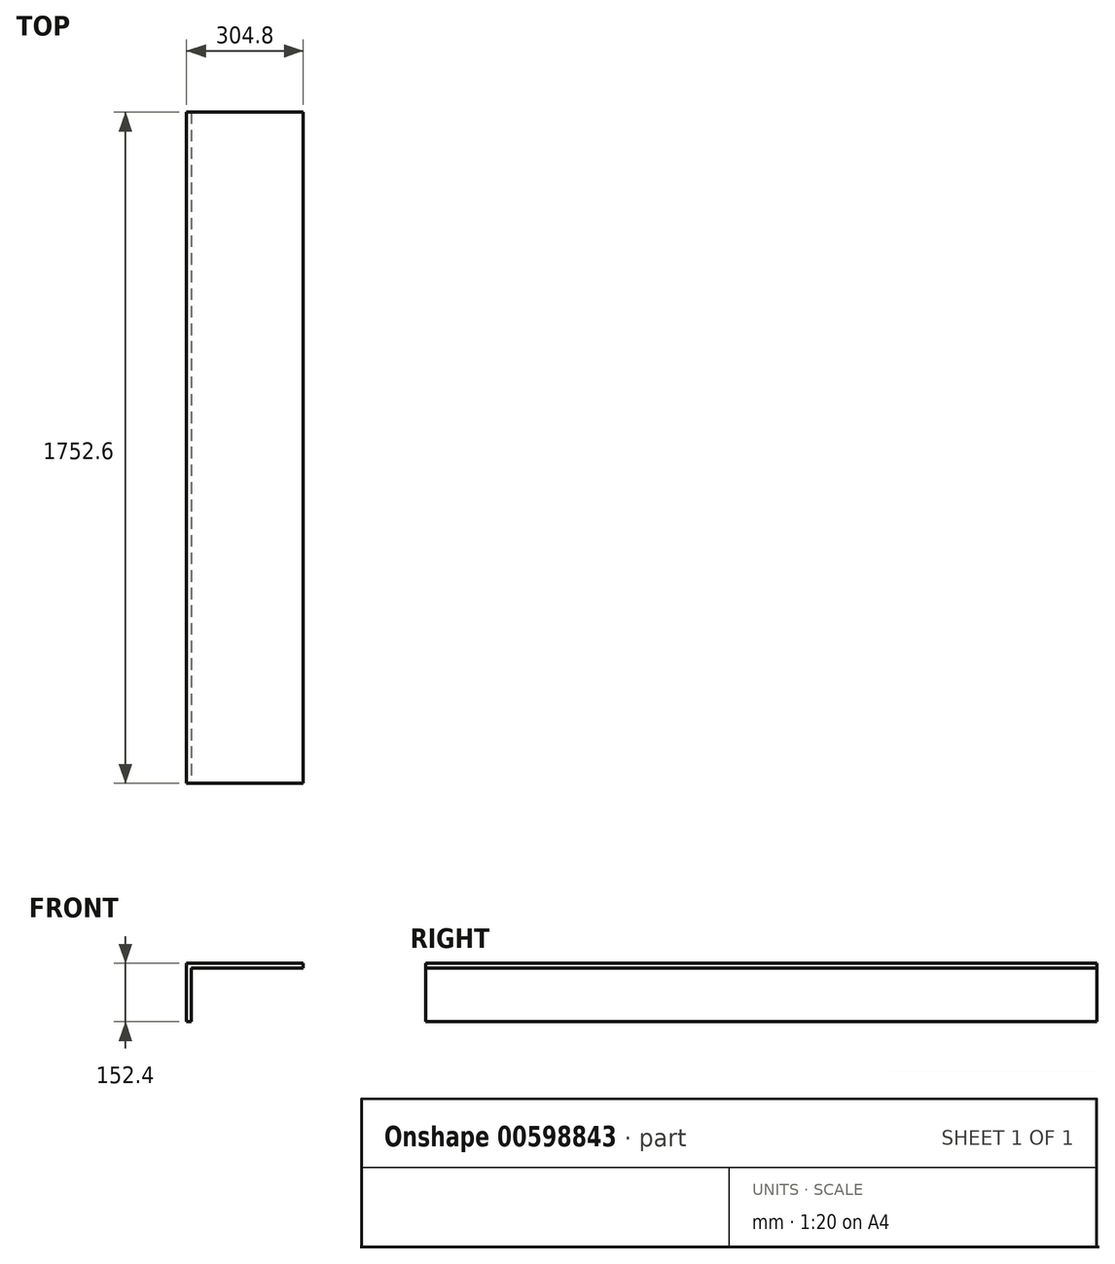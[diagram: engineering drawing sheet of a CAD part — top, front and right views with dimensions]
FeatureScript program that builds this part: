
annotation { "Feature Type Name" : "Feature", "Feature Type Description" : "" }
export const myFeature = defineFeature(function(context is Context, id is Id, definition is map)
    precondition{}
    {
        {
            var Q0;
            Q0=qCreatedBy(makeId("Front.planeOp"),FACE);
            var sketch = newSketch(context, id + "F0", { "sketchPlane" : qUnion([Q0])});
            skLineSegment(sketch, "E0", {"start": v(-143.19, 29.27) * mm, "end": v(161.61, 29.27) * mm});
            skLineSegment(sketch, "E1", {"start": v(161.61, 29.27) * mm, "end": v(161.61, 16.57) * mm});
            skLineSegment(sketch, "E2", {"start": v(-143.19, 29.27) * mm, "end": v(-143.19, -123.13) * mm});
            skLineSegment(sketch, "E3", {"start": v(-143.19, -123.13) * mm, "end": v(-130.49, -123.13) * mm});
            skPoint(sketch, "E4.endSnap0", {"position": v(161.61, 22.92) * mm});
            skLineSegment(sketch, "E5", {"start": v(161.61, 16.57) * mm, "end": v(-130.49, 16.57) * mm});
            skLineSegment(sketch, "E6", {"start": v(-130.49, 16.57) * mm, "end": v(-130.49, -123.13) * mm});
            skSolve(sketch);
        }
        {
            var Q0;
            Q0=makeQuery(id+"F0.imprint","IMPRINT",FACE,{"disambiguationData":[TD([[makeQuery(id+"F0.imprint","IMPRINT",EDGE,{"derivedFrom":sQuery(id+"F0.wireOp",EDGE,"E0")}),-1.0]])]});
            extrude(context, id + "F1", {"entities" : qUnion([Q0]), "oppositeDirection" : true, "depth" : 1752.6 * mm, "offsetDistance" : 25.4 * mm});
        }
    });
